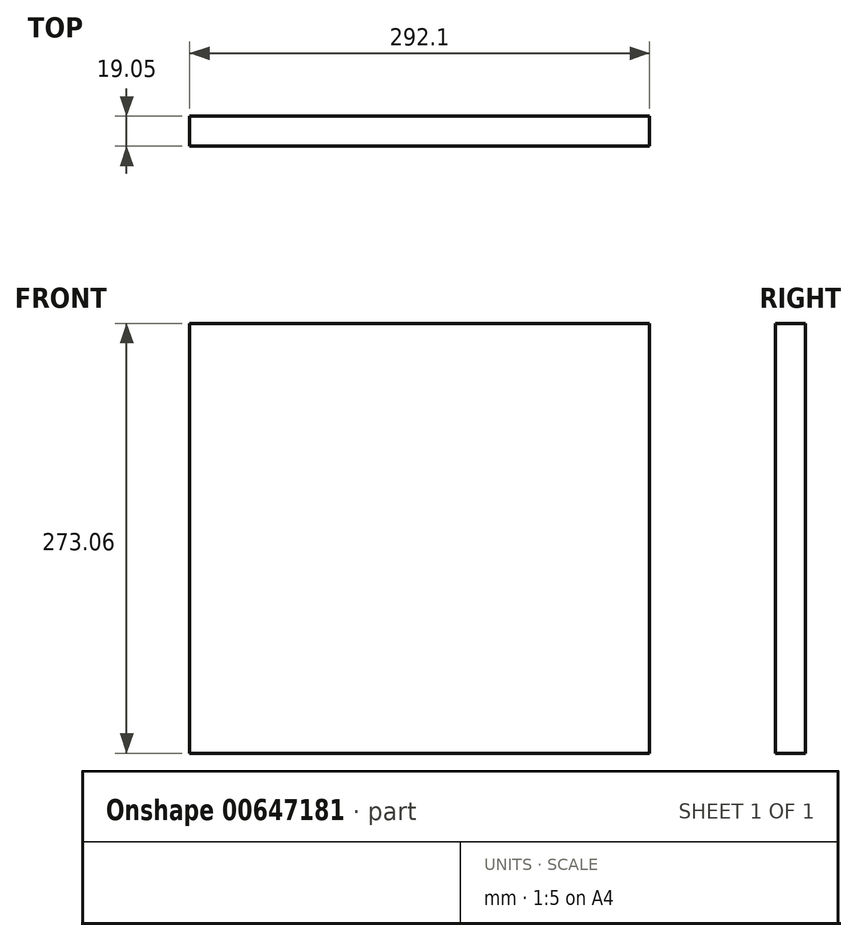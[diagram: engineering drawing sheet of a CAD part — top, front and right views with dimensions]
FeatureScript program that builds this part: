
annotation { "Feature Type Name" : "Feature", "Feature Type Description" : "" }
export const myFeature = defineFeature(function(context is Context, id is Id, definition is map)
    precondition{}
    {
        {
            var Q0;
            Q0=qCreatedBy(makeId("Front.planeOp"),FACE);
            var sketch = newSketch(context, id + "F0", { "sketchPlane" : qUnion([Q0])});
            skLineSegment(sketch, "E0.bottom", {"start": v(-146.05, 136.53) * mm, "end": v(146.05, 136.53) * mm});
            skLineSegment(sketch, "E0.top", {"start": v(-146.05, -136.52) * mm, "end": v(146.05, -136.52) * mm});
            skLineSegment(sketch, "E0.left", {"start": v(-146.05, 136.53) * mm, "end": v(-146.05, -136.52) * mm});
            skLineSegment(sketch, "E0.right", {"start": v(146.05, 136.53) * mm, "end": v(146.05, -136.52) * mm});
            skPoint(sketch, "E0.middle", {"position": v(0, 0) * mm});
            skSolve(sketch);
        }
        {
            var Q0;
            Q0=makeQuery(id+"F0.imprint","IMPRINT",FACE,{"disambiguationData":[TD([[makeQuery(id+"F0.imprint","IMPRINT",EDGE,{"derivedFrom":sQuery(id+"F0.wireOp",EDGE,"E0.bottom")}),-1.0]])]});
            extrude(context, id + "F1", {"entities" : qUnion([Q0]), "depth" : 19.05 * mm, "offsetDistance" : 25.4 * mm});
        }
    });
